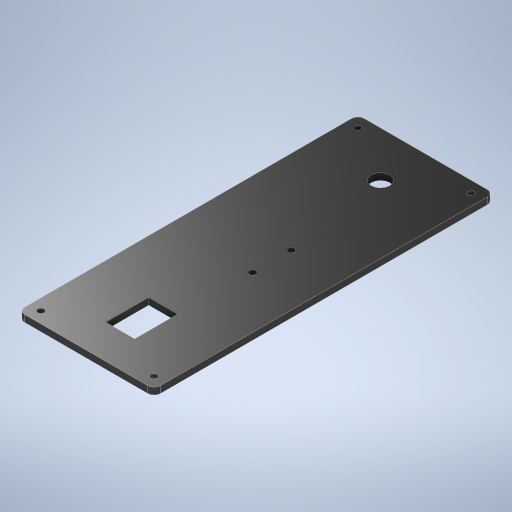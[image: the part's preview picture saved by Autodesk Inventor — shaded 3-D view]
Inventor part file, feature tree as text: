
AUTODESK INVENTOR PART (.ipt)
format: ipt  version: 2023 (Build 270158000, 158)  size: 273,408 bytes
history: native  units: in
note: dims shown in document units (in); Inventor stores cm internally (conversion verified against a paired STEP export)
features: other x3, extrude x2, sketch x1
ambient origin geometry x8: Origin, YZ Plane, XZ Plane, XY Plane, X Axis, Y Axis, Z Axis, Center Point
bodies: Solid1 (feature_tree)
feature tree (6):
  other  "MatTren.ipt"
  extrude  "Extrusion1"  Depth=0.3937in
  extrude  "Extrusion2"  Depth=0.5906in
  other  "Solid1::MatTren.ipt"
  other  "TaggingFeature1"
  sketch  "Sketch1"  dims[d0=0.3937in d1=0.252in d2=0.5906in d3=0.252in d4=0.748in d5=0.3937in d6=0.0in d7=0.7874in d8=0.3268in d9=0.3937in d10=0.0in]
